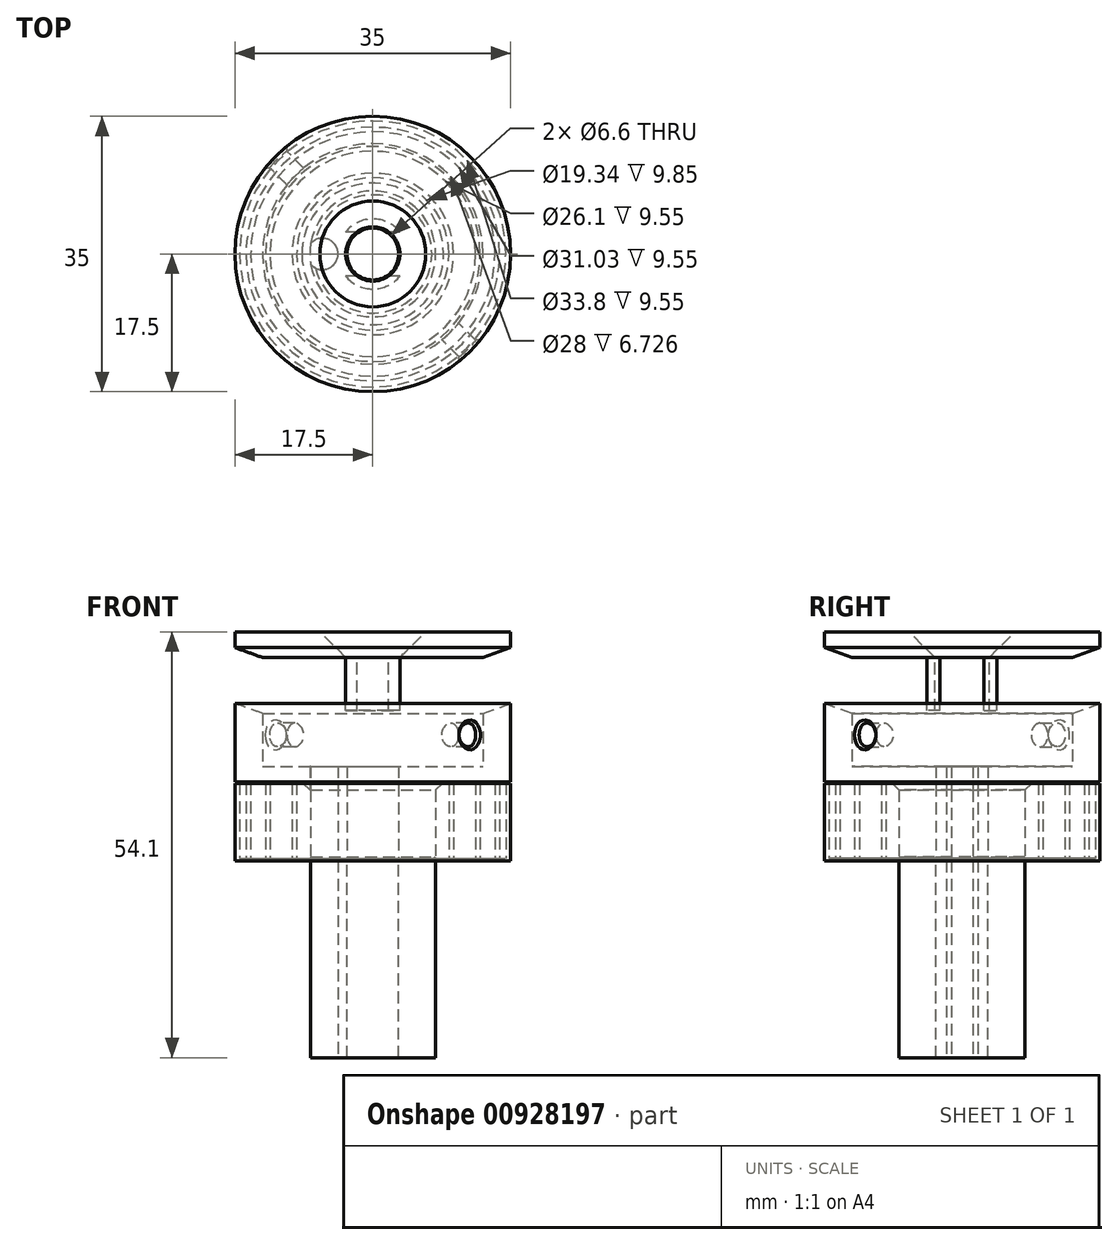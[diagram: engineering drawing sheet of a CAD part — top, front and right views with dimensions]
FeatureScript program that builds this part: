
annotation { "Feature Type Name" : "Feature", "Feature Type Description" : "" }
export const myFeature = defineFeature(function(context is Context, id is Id, definition is map)
    precondition{}
    {
        {
            var Q0;
            Q0=qCreatedBy(makeId("Front.planeOp"),FACE);
            var sketch = newSketch(context, id + "F0", { "sketchPlane" : qUnion([Q0])});
            skLineSegment(sketch, "E0", {"start": v(-8, 3.73) * mm, "end": v(-8, 13.73) * mm});
            skLineSegment(sketch, "E1", {"start": v(-8, 13.73) * mm, "end": v(-17.5, 13.73) * mm});
            skLineSegment(sketch, "E2", {"start": v(-17.5, 13.73) * mm, "end": v(-17.5, 23.73) * mm});
            skLineSegment(sketch, "E3", {"start": v(-3.3, 3.73) * mm, "end": v(-8, 3.73) * mm});
            skLineSegment(sketch, "E4", {"start": v(-14, 22.46) * mm, "end": v(-14, 15.73) * mm});
            skLineSegment(sketch, "E5", {"start": v(-14, 15.73) * mm, "end": v(-3.3, 15.73) * mm});
            skLineSegment(sketch, "E6", {"start": v(0, -9.2) * mm, "end": v(0, 30.16) * mm, "construction": true});
            skLineSegment(sketch, "E7", {"start": v(-3.3, 15.73) * mm, "end": v(-3.3, 3.73) * mm});
            skLineSegment(sketch, "E8", {"start": v(-17.5, 23.73) * mm, "end": v(-14, 22.46) * mm});
            skLineSegment(sketch, "E9", {"start": v(-8.7, 3.73) * mm, "end": v(-35.04, 3.73) * mm, "construction": true});
            skLineSegment(sketch, "E10.bottom", {"start": v(-17.5, 3.73) * mm, "end": v(-16.9, 3.73) * mm});
            skLineSegment(sketch, "E10.top", {"start": v(-17.5, 13.58) * mm, "end": v(-16.9, 13.58) * mm});
            skLineSegment(sketch, "E10.left", {"start": v(-17.5, 3.73) * mm, "end": v(-17.5, 13.58) * mm});
            skLineSegment(sketch, "E10.right", {"start": v(-16.9, 3.73) * mm, "end": v(-16.9, 13.58) * mm});
            skLineSegment(sketch, "E11.bottom", {"start": v(-10.27, 3.73) * mm, "end": v(-9.67, 3.73) * mm});
            skLineSegment(sketch, "E11.top", {"start": v(-10.27, 13.58) * mm, "end": v(-9.67, 13.58) * mm});
            skLineSegment(sketch, "E11.left", {"start": v(-10.27, 3.73) * mm, "end": v(-10.27, 13.58) * mm});
            skLineSegment(sketch, "E11.right", {"start": v(-9.67, 3.73) * mm, "end": v(-9.67, 13.58) * mm});
            skLineSegment(sketch, "E12.bottom", {"start": v(-13.65, 3.73) * mm, "end": v(-13.05, 3.73) * mm});
            skLineSegment(sketch, "E12.top", {"start": v(-13.65, 13.58) * mm, "end": v(-13.05, 13.58) * mm});
            skLineSegment(sketch, "E12.left", {"start": v(-13.65, 3.73) * mm, "end": v(-13.65, 13.58) * mm});
            skLineSegment(sketch, "E12.right", {"start": v(-13.05, 3.73) * mm, "end": v(-13.05, 13.58) * mm});
            skLineSegment(sketch, "E13.bottom", {"start": v(-17.5, 3.73) * mm, "end": v(-9.67, 3.73) * mm});
            skLineSegment(sketch, "E13.top", {"start": v(-17.5, 4.03) * mm, "end": v(-9.67, 4.03) * mm});
            skLineSegment(sketch, "E13.left", {"start": v(-17.5, 3.73) * mm, "end": v(-17.5, 4.03) * mm});
            skLineSegment(sketch, "E13.right", {"start": v(-9.67, 3.73) * mm, "end": v(-9.67, 4.03) * mm});
            skLineSegment(sketch, "E14.bottom", {"start": v(-16.11, 13.58) * mm, "end": v(-15.51, 13.58) * mm});
            skLineSegment(sketch, "E14.top", {"start": v(-16.11, 3.73) * mm, "end": v(-15.51, 3.73) * mm});
            skLineSegment(sketch, "E14.left", {"start": v(-16.11, 13.58) * mm, "end": v(-16.11, 3.73) * mm});
            skLineSegment(sketch, "E14.right", {"start": v(-15.51, 13.58) * mm, "end": v(-15.51, 3.73) * mm});
            skSolve(sketch);
        }
        {
            var Q0;
            Q0 = qSketchRegion(id + "F0", true);
            var Q1;
            Q1=sQuery(id+"F0.wireOp",EDGE,"E6");
            revolve(context, id + "F1", {"surfaceOperationType" : NewSurfaceOperationType.NEW, "entities" : qUnion([Q0]), "axis" : qUnion([Q1]), "revolveType" : RevolveType.FULL});
        }
        {
            var Q0;
            Q0=qCreatedBy(makeId("Right.planeOp"),FACE);
            var sketch = newSketch(context, id + "F2", { "sketchPlane" : qUnion([Q0])});
            skLineSegment(sketch, "E15", {"start": v(0, -16.71) * mm, "end": v(0, 42.1) * mm, "construction": true});
            skSolve(sketch);
        }
        {
            var Q0;
            Q0=qCreatedBy(makeId("Right.planeOp"),FACE);
            var Q1;
            Q1=sQuery(id+"F2.wireOp",EDGE,"E15");
            cPlane(context, id + "F3", {"entities" : qUnion([Q0, Q1]), "cplaneType" : CPlaneType.LINE_ANGLE, "offset" : 25 * mm, "angle" : 45 * degree, "oppositeDirection" : true, "width" : 150 * mm, "height" : 150 * mm});
        }
        {
            var Q0;
            Q0=qCreatedBy(id+"F3.planeOp",FACE);
            var sketch = newSketch(context, id + "F4", { "sketchPlane" : qUnion([Q0])});
            skCircle(sketch, "E16", {"center": v(0, 19.73) * mm, "radius": 1.5 * mm});
            skSolve(sketch);
        }
        {
            var Q0;
            Q0 = qSketchRegion(id + "F4", true);
            extrude(context, id + "F5", {"entities" : qUnion([Q0]), "operationType" : NewBodyOperationType.REMOVE, "endBound" : BoundingType.SYMMETRIC, "oppositeDirection" : true, "depth" : 51.6 * mm, "offsetDistance" : 25 * mm});
        }
        {
            var Q0;
            Q0=makeQuery(id+"F1.opRevolve","SWEPT_EDGE",EDGE,{"disambiguationData":[OSD([sQuery(id+"F0.wireOp",EDGE,"E0"),sQuery(id+"F0.wireOp",EDGE,"E3")])]});
            chamfer(context, id + "F6", {"entities" : qUnion([Q0]), "width" : 0.5 * mm, "tangentPropagation" : true});
        }
        {
            var Q0;
            Q0=makeQuery(id+"F1.opRevolve","SWEPT_EDGE",EDGE,{"disambiguationData":[OSD([sQuery(id+"F0.wireOp",EDGE,"E0"),sQuery(id+"F0.wireOp",EDGE,"E1")])]});
            chamfer(context, id + "F7", {"entities" : qUnion([Q0]), "width" : 1 * mm, "tangentPropagation" : true});
        }
        {
            var Q0;
            Q0=makeQuery(id+"F1.opRevolve","SWEPT_FACE",FACE,{"disambiguationData":[OSD([sQuery(id+"F0.wireOp",EDGE,"E3")])]});
            var sketch = newSketch(context, id + "F8", { "sketchPlane" : qUnion([Q0])});
            skCircle(sketch, "E17.0", {"center": v(0, 0) * mm, "radius": 3.3 * mm});
            skCircle(sketch, "E18.0", {"center": v(0, 0) * mm, "radius": 8 * mm});
            skSolve(sketch);
        }
        {
            var Q0;
            Q0 = qSketchRegion(id + "F8", true);
            extrude(context, id + "F9", {"entities" : qUnion([Q0]), "depth" : 25 * mm, "offsetDistance" : 25 * mm});
        }
        {
            var Q0;
            Q0=makeQuery(id+"F9.opExtrude","CAP_FACE",FACE,{"disambiguationData":[OSD([sQuery(id+"F8.wireOp",EDGE,"20238de4-e1c5-4668-b5fc-17e9d4727b8c.0"),sQuery(id+"F8.wireOp",EDGE,"E17.0")])],"isStart":false});
            var sketch = newSketch(context, id + "F10", { "sketchPlane" : qUnion([Q0])});
            skArc(sketch, "E19", {"start": v(-7.88, -1.36) * mm, "mid": v(-4.42, 0) * mm, "end": v(-7.88, 1.36) * mm});
            skArc(sketch, "E20.0", {"start": v(-7.88, 1.36) * mm, "mid": v(-8, 0) * mm, "end": v(-7.88, -1.36) * mm});
            skSolve(sketch);
        }
        {
            var Q0;
            Q0 = qSketchRegion(id + "F10", true);
            extrude(context, id + "F11", {"entities" : qUnion([Q0]), "operationType" : NewBodyOperationType.REMOVE, "endBound" : BoundingType.THROUGH_ALL, "oppositeDirection" : true, "depth" : 25 * mm, "offsetDistance" : 25 * mm});
        }
        {
            var Q0;
            Q0=qCreatedBy(makeId("Front.planeOp"),FACE);
            var sketch = newSketch(context, id + "F12", { "sketchPlane" : qUnion([Q0])});
            skLineSegment(sketch, "E21", {"start": v(-17.5, 32.83) * mm, "end": v(-17.5, 30.83) * mm});
            skLineSegment(sketch, "E22", {"start": v(-14, 29.56) * mm, "end": v(0, 29.56) * mm});
            skLineSegment(sketch, "E23", {"start": v(0, 32.83) * mm, "end": v(-17.5, 32.83) * mm});
            skLineSegment(sketch, "E24", {"start": v(0, 8.31) * mm, "end": v(0, 39.5) * mm, "construction": true});
            skLineSegment(sketch, "E25", {"start": v(0, 29.56) * mm, "end": v(0, 32.83) * mm});
            skLineSegment(sketch, "E26", {"start": v(-14, 29.56) * mm, "end": v(-17.5, 30.83) * mm});
            skSolve(sketch);
        }
        {
            var Q0;
            Q0 = qSketchRegion(id + "F12", true);
            var Q1;
            Q1=sQuery(id+"F12.wireOp",EDGE,"E24");
            revolve(context, id + "F13", {"surfaceOperationType" : NewSurfaceOperationType.NEW, "entities" : qUnion([Q0]), "axis" : qUnion([Q1]), "revolveType" : RevolveType.FULL});
        }
        {
            var Q0;
            Q0=makeQuery(id+"F13.opRevolve","SWEPT_FACE",FACE,{"disambiguationData":[OSD([sQuery(id+"F12.wireOp",EDGE,"E23")])]});
            var sketch = newSketch(context, id + "F14", { "sketchPlane" : qUnion([Q0])});
            skPoint(sketch, "E27", {"position": v(0, 0) * mm});
            skSolve(sketch);
        }
        {
            var Q0;
            Q0=sQuery(id+"F14.wireOp",VERTEX,"E27");
            var Q1;
            Q1=makeQuery(id+"F13.opRevolve","SWEPT_BODY",BODY,{"disambiguationData":[OSD([sQuery(id+"F12.wireOp",EDGE,"E21"),sQuery(id+"F12.wireOp",EDGE,"qeaFNRgR-eucZ-NjJQ-QIDL-RzUJUSbK2mfH"),sQuery(id+"F12.wireOp",EDGE,"1ZPHNXAn-A5CA-kr2Y-H85I-OgsECEQN20dQ"),sQuery(id+"F12.wireOp",EDGE,"E22"),sQuery(id+"F12.wireOp",EDGE,"E23"),sQuery(id+"F12.wireOp",EDGE,"E25")])]});
            hole(context, id + "F15", {"style" : HoleStyle.C_SINK, "endStyle" : HoleEndStyle.THROUGH, "standardTappedOrClearance" : lookupTablePath({ "fit" : "Normal", "standard" : "ISO", "size" : "M6", "type" : "Clearance" }), "standardBlindInLast" : lookupTablePath({ "fit" : "Normal", "standard" : "ISO", "size" : "M6", "type" : "Clearance" }), "holeDiameter" : 6.6 * mm, "cSinkDiameter" : 13.44 * mm, "cSinkAngle" : 90 * degree, "majorDiameter" : 5 * mm, "tappedDepth" : 7.6 * mm, "tapClearance" : 3, "startFromSketch" : true, "locations" : qUnion([Q0]), "scope" : qUnion([Q1])});
        }
        {
            var Q0;
            Q0=makeQuery(id+"FZqVPAtDpOuDheF_2.5.F5.boolean.opBoolean","INTERSECT",EDGE,{"disambiguationData":[OD(0.0)],"derivedFrom":[makeQuery(id+"F1.opRevolve","SWEPT_FACE",FACE,{"disambiguationData":[OSD([sQuery(id+"F0.wireOp",EDGE,"E2")])]}),makeQuery(id+"FZqVPAtDpOuDheF_2.5.F5.opExtrude","SWEPT_FACE",FACE,{"disambiguationData":[OSD([sQuery(id+"F4.wireOp",EDGE,"E16")])]})]});
            var Q1;
            Q1=makeQuery(id+"FZqVPAtDpOuDheF_2.4.F5.boolean.opBoolean","INTERSECT",EDGE,{"disambiguationData":[OD(0.0)],"derivedFrom":[makeQuery(id+"F1.opRevolve","SWEPT_FACE",FACE,{"disambiguationData":[OSD([sQuery(id+"F0.wireOp",EDGE,"E2")])]}),makeQuery(id+"FZqVPAtDpOuDheF_2.4.F5.opExtrude","SWEPT_FACE",FACE,{"disambiguationData":[OSD([sQuery(id+"F4.wireOp",EDGE,"E16")])]})]});
            var Q2;
            Q2=makeQuery(id+"FZqVPAtDpOuDheF_2.3.F5.boolean.opBoolean","INTERSECT",EDGE,{"disambiguationData":[OD(0.0)],"derivedFrom":[makeQuery(id+"F1.opRevolve","SWEPT_FACE",FACE,{"disambiguationData":[OSD([sQuery(id+"F0.wireOp",EDGE,"E2")])]}),makeQuery(id+"FZqVPAtDpOuDheF_2.3.F5.opExtrude","SWEPT_FACE",FACE,{"disambiguationData":[OSD([sQuery(id+"F4.wireOp",EDGE,"E16")])]})]});
            var Q3;
            Q3=makeQuery(id+"FZqVPAtDpOuDheF_2.2.F5.boolean.opBoolean","INTERSECT",EDGE,{"disambiguationData":[OD(1.0)],"derivedFrom":[makeQuery(id+"F1.opRevolve","SWEPT_FACE",FACE,{"disambiguationData":[OSD([sQuery(id+"F0.wireOp",EDGE,"E2")])]}),makeQuery(id+"FZqVPAtDpOuDheF_2.2.F5.opExtrude","SWEPT_FACE",FACE,{"disambiguationData":[OSD([sQuery(id+"F4.wireOp",EDGE,"E16")])]})]});
            var Q4;
            Q4=makeQuery(id+"FZqVPAtDpOuDheF_2.1.F5.boolean.opBoolean","INTERSECT",EDGE,{"disambiguationData":[OD(1.0)],"derivedFrom":[makeQuery(id+"F1.opRevolve","SWEPT_FACE",FACE,{"disambiguationData":[OSD([sQuery(id+"F0.wireOp",EDGE,"E2")])]}),makeQuery(id+"FZqVPAtDpOuDheF_2.1.F5.opExtrude","SWEPT_FACE",FACE,{"disambiguationData":[OSD([sQuery(id+"F4.wireOp",EDGE,"E16")])]})]});
            var Q5;
            Q5=makeQuery(id+"F5.boolean.opBoolean","INTERSECT",EDGE,{"disambiguationData":[OD(1.0)],"derivedFrom":[makeQuery(id+"F1.opRevolve","SWEPT_FACE",FACE,{"disambiguationData":[OSD([sQuery(id+"F0.wireOp",EDGE,"E2")])]}),makeQuery(id+"F5.opExtrude","SWEPT_FACE",FACE,{"disambiguationData":[OSD([sQuery(id+"F4.wireOp",EDGE,"E16")])]})]});
            var Q6;
            Q6=makeQuery(id+"F5.boolean.opBoolean","INTERSECT",EDGE,{"disambiguationData":[OD(0.0)],"derivedFrom":[makeQuery(id+"F1.opRevolve","SWEPT_FACE",FACE,{"disambiguationData":[OSD([sQuery(id+"F0.wireOp",EDGE,"E2")])]}),makeQuery(id+"F5.opExtrude","SWEPT_FACE",FACE,{"disambiguationData":[OSD([sQuery(id+"F4.wireOp",EDGE,"E16")])]})]});
            var Q7;
            Q7=makeQuery(id+"FZqVPAtDpOuDheF_2.1.F5.boolean.opBoolean","INTERSECT",EDGE,{"disambiguationData":[OD(0.0)],"derivedFrom":[makeQuery(id+"F1.opRevolve","SWEPT_FACE",FACE,{"disambiguationData":[OSD([sQuery(id+"F0.wireOp",EDGE,"E2")])]}),makeQuery(id+"FZqVPAtDpOuDheF_2.1.F5.opExtrude","SWEPT_FACE",FACE,{"disambiguationData":[OSD([sQuery(id+"F4.wireOp",EDGE,"E16")])]})]});
            var Q8;
            Q8=makeQuery(id+"FZqVPAtDpOuDheF_2.2.F5.boolean.opBoolean","INTERSECT",EDGE,{"disambiguationData":[OD(0.0)],"derivedFrom":[makeQuery(id+"F1.opRevolve","SWEPT_FACE",FACE,{"disambiguationData":[OSD([sQuery(id+"F0.wireOp",EDGE,"E2")])]}),makeQuery(id+"FZqVPAtDpOuDheF_2.2.F5.opExtrude","SWEPT_FACE",FACE,{"disambiguationData":[OSD([sQuery(id+"F4.wireOp",EDGE,"E16")])]})]});
            var Q9;
            Q9=makeQuery(id+"FZqVPAtDpOuDheF_2.3.F5.boolean.opBoolean","INTERSECT",EDGE,{"disambiguationData":[OD(1.0)],"derivedFrom":[makeQuery(id+"F1.opRevolve","SWEPT_FACE",FACE,{"disambiguationData":[OSD([sQuery(id+"F0.wireOp",EDGE,"E2")])]}),makeQuery(id+"FZqVPAtDpOuDheF_2.3.F5.opExtrude","SWEPT_FACE",FACE,{"disambiguationData":[OSD([sQuery(id+"F4.wireOp",EDGE,"E16")])]})]});
            var Q10;
            Q10=makeQuery(id+"FZqVPAtDpOuDheF_2.4.F5.boolean.opBoolean","INTERSECT",EDGE,{"disambiguationData":[OD(1.0)],"derivedFrom":[makeQuery(id+"F1.opRevolve","SWEPT_FACE",FACE,{"disambiguationData":[OSD([sQuery(id+"F0.wireOp",EDGE,"E2")])]}),makeQuery(id+"FZqVPAtDpOuDheF_2.4.F5.opExtrude","SWEPT_FACE",FACE,{"disambiguationData":[OSD([sQuery(id+"F4.wireOp",EDGE,"E16")])]})]});
            var Q11;
            Q11=makeQuery(id+"FZqVPAtDpOuDheF_2.5.F5.boolean.opBoolean","INTERSECT",EDGE,{"disambiguationData":[OD(1.0)],"derivedFrom":[makeQuery(id+"F1.opRevolve","SWEPT_FACE",FACE,{"disambiguationData":[OSD([sQuery(id+"F0.wireOp",EDGE,"E2")])]}),makeQuery(id+"FZqVPAtDpOuDheF_2.5.F5.opExtrude","SWEPT_FACE",FACE,{"disambiguationData":[OSD([sQuery(id+"F4.wireOp",EDGE,"E16")])]})]});
            chamfer(context, id + "F16", {"entities" : qUnion([Q0, Q1, Q2, Q3, Q4, Q5, Q6, Q7, Q8, Q9, Q10, Q11]), "width" : 0.4 * mm, "tangentPropagation" : true});
        }
        {
            var Q0;
            Q0=makeQuery(id+"F13.opRevolve","SWEPT_FACE",FACE,{"disambiguationData":[OSD([sQuery(id+"F12.wireOp",EDGE,"E22")])]});
            var sketch = newSketch(context, id + "F17", { "sketchPlane" : qUnion([Q0])});
            skArc(sketch, "E28", {"start": v(-3.46, -2.8) * mm, "mid": v(0, -4.45) * mm, "end": v(3.46, -2.8) * mm});
            skArc(sketch, "E29.0", {"start": v(-2.02, -2.8) * mm, "mid": v(0, -3.45) * mm, "end": v(2.02, -2.8) * mm});
            skLineSegment(sketch, "E30.bottom", {"start": v(3.46, -2.8) * mm, "end": v(2.02, -2.8) * mm});
            skLineSegment(sketch, "E30.top", {"start": v(3.46, 2.8) * mm, "end": v(2.02, 2.8) * mm});
            skPoint(sketch, "E31.orphan", {"position": v(-6.4, 2.8) * mm});
            skPoint(sketch, "E32.orphan", {"position": v(-6.4, -2.8) * mm});
            skArc(sketch, "E33.trimOffspring", {"start": v(2.02, 2.8) * mm, "mid": v(0, 3.45) * mm, "end": v(-2.02, 2.8) * mm});
            skArc(sketch, "E34.trimOffspring", {"start": v(3.46, 2.8) * mm, "mid": v(0, 4.45) * mm, "end": v(-3.46, 2.8) * mm});
            skPoint(sketch, "E35.orphan", {"position": v(6.4, 2.8) * mm});
            skPoint(sketch, "E36.orphan", {"position": v(6.4, -2.8) * mm});
            skLineSegment(sketch, "E37.trimOffspring", {"start": v(-2.02, 2.8) * mm, "end": v(-3.46, 2.8) * mm});
            skLineSegment(sketch, "E38.trimOffspring", {"start": v(-2.02, -2.8) * mm, "end": v(-3.46, -2.8) * mm});
            skSolve(sketch);
        }
        {
            var Q0;
            Q0 = qSketchRegion(id + "F17", true);
            extrude(context, id + "F18", {"entities" : qUnion([Q0]), "operationType" : NewBodyOperationType.ADD, "depth" : 6.73 * mm, "offsetDistance" : 25 * mm});
        }
    });
